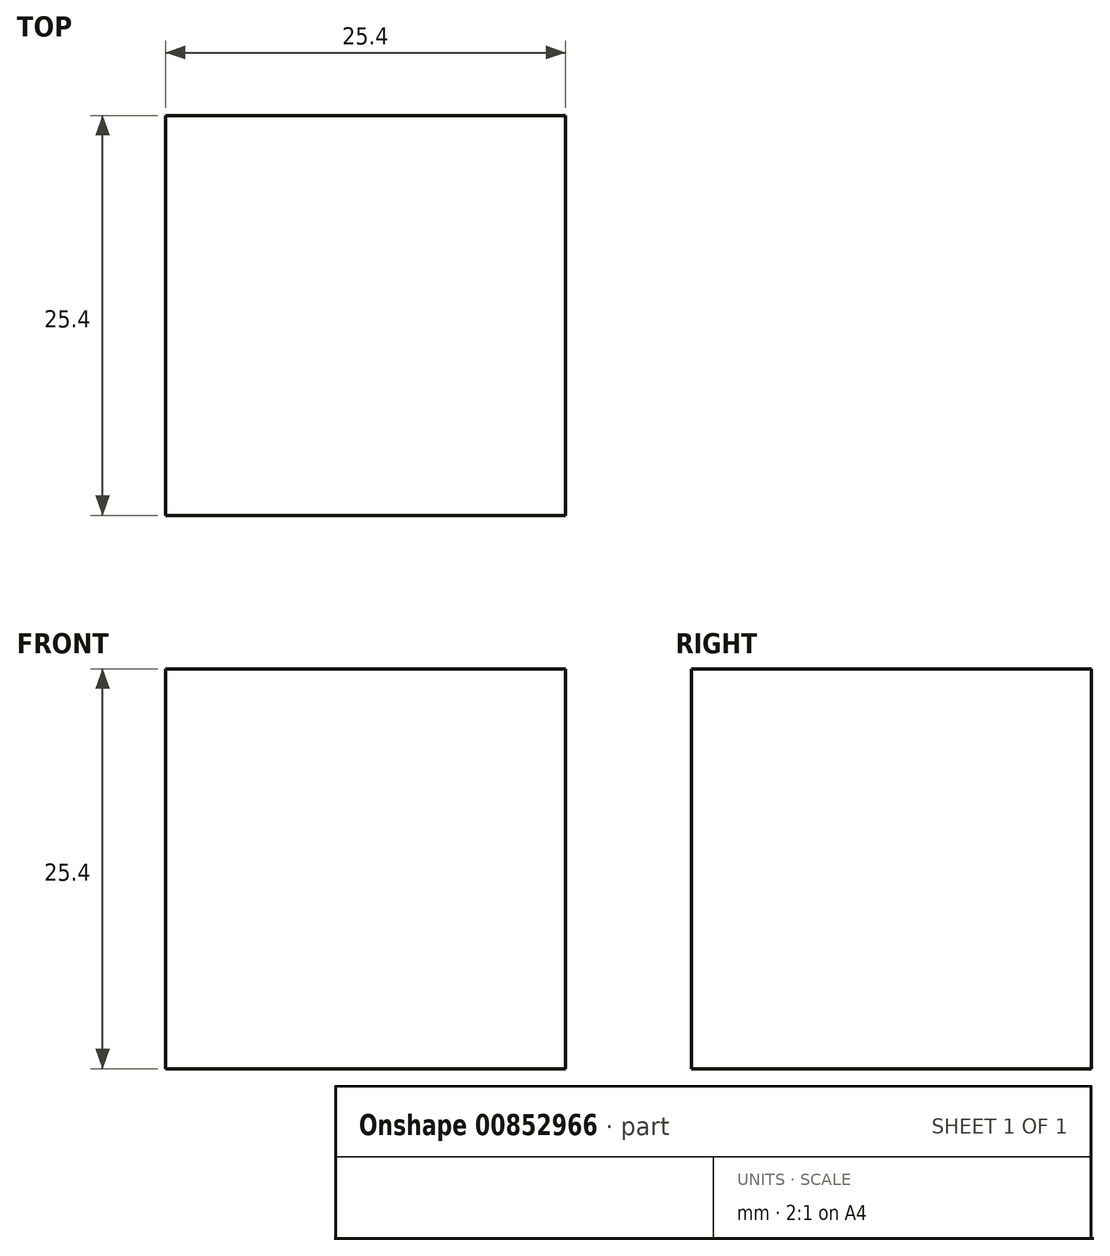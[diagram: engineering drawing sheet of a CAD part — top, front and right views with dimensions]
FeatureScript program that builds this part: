
annotation { "Feature Type Name" : "Feature", "Feature Type Description" : "" }
export const myFeature = defineFeature(function(context is Context, id is Id, definition is map)
    precondition{}
    {
        {
            var Q0;
            Q0=qCreatedBy(makeId("Top.planeOp"),FACE);
            var sketch = newSketch(context, id + "F0", { "sketchPlane" : qUnion([Q0])});
            skLineSegment(sketch, "E0.bottom", {"start": v(0, 0) * mm, "end": v(-25.4, 0) * mm});
            skLineSegment(sketch, "E0.top", {"start": v(0, 25.4) * mm, "end": v(-25.4, 25.4) * mm});
            skLineSegment(sketch, "E0.left", {"start": v(0, 0) * mm, "end": v(0, 25.4) * mm});
            skLineSegment(sketch, "E0.right", {"start": v(-25.4, 0) * mm, "end": v(-25.4, 25.4) * mm});
            skSolve(sketch);
        }
        {
            var Q0;
            Q0=makeQuery(id+"F0.imprint","IMPRINT",FACE,{"disambiguationData":[TD([[makeQuery(id+"F0.imprint","IMPRINT",EDGE,{"derivedFrom":sQuery(id+"F0.wireOp",EDGE,"E0.bottom")}),-1.0]])]});
            extrude(context, id + "F1", {"entities" : qUnion([Q0]), "depth" : 25.4 * mm, "offsetDistance" : 25.4 * mm});
        }
    });
